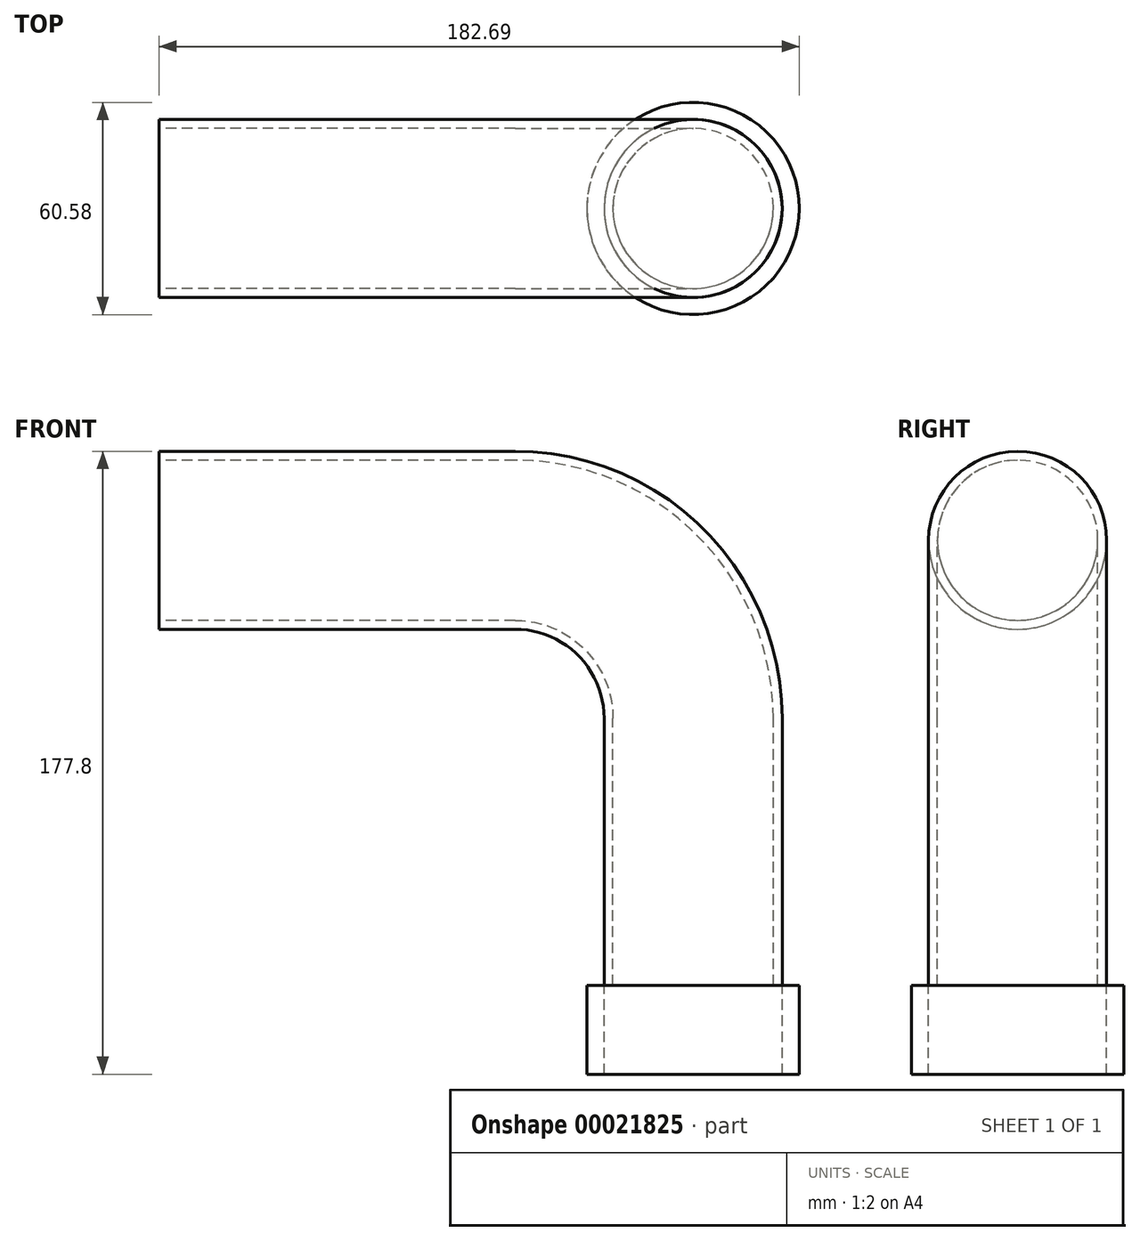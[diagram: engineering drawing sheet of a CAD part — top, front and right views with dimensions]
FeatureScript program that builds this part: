
annotation { "Feature Type Name" : "Feature", "Feature Type Description" : "" }
export const myFeature = defineFeature(function(context is Context, id is Id, definition is map)
    precondition{}
    {
        {
            var Q0;
            Q0=qCreatedBy(makeId("Top.planeOp"),FACE);
            var sketch = newSketch(context, id + "F0", { "sketchPlane" : qUnion([Q0])});
            skCircle(sketch, "E0", {"center": v(0, 0) * mm, "radius": 25.4 * mm});
            skSolve(sketch);
        }
        {
            var Q0;
            Q0=qCreatedBy(makeId("Front.planeOp"),FACE);
            var sketch = newSketch(context, id + "F1", { "sketchPlane" : qUnion([Q0])});
            skLineSegment(sketch, "E1", {"start": v(0, 0) * mm, "end": v(0, 76.2) * mm});
            skLineSegment(sketch, "E2", {"start": v(-50.8, 127) * mm, "end": v(-152.4, 127) * mm});
            skPoint(sketch, "E3.visualSharp", {"position": v(0, 127) * mm});
            skArc(sketch, "E3.filletArc", {"start": v(0, 76.2) * mm, "mid": v(-14.88, 112.12) * mm, "end": v(-50.8, 127) * mm});
            skSolve(sketch);
        }
        {
            var Q0;
            Q0=makeQuery(id+"F0.imprint","IMPRINT",FACE,{"disambiguationData":[TD([[makeQuery(id+"F0.imprint","IMPRINT",EDGE,{"derivedFrom":sQuery(id+"F0.wireOp",EDGE,"E0")}),1.0]])]});
            var Q1;
            Q1=sQuery(id+"F0.wireOp",EDGE,"E0");
            var Q2;
            Q2=sQuery(id+"F1.wireOp",EDGE,"E1");
            var Q3;
            Q3=sQuery(id+"F1.wireOp",EDGE,"E3.filletArc");
            var Q4;
            Q4=sQuery(id+"F1.wireOp",EDGE,"E2");
            sweep(context, id + "F2", {"profiles" : qUnion([Q0]), "surfaceProfiles" : qUnion([Q1]), "path" : qUnion([Q2, Q3, Q4])});
        }
        {
            var Q0;
            Q0=makeQuery(id+"F2.opSweep","CAP_FACE",FACE,{"disambiguationData":[OSD([sQuery(id+"F0.wireOp",EDGE,"E0"),sQuery(id+"F1.wireOp",VERTEX,"E2.end")])],"isStart":false});
            var Q1;
            Q1=makeQuery(id+"F2.opSweep","CAP_FACE",FACE,{"disambiguationData":[OSD([sQuery(id+"F0.wireOp",EDGE,"E0"),sQuery(id+"F1.wireOp",VERTEX,"E1.start")])],"isStart":true});
            shell(context, id + "F3", {"entities" : qUnion([Q0, Q1]), "thickness" : 2.54 * mm});
        }
        {
            var Q0;
            Q0=makeQuery(id+"F2.opSweep","CAP_FACE",FACE,{"disambiguationData":[OSD([sQuery(id+"F0.wireOp",EDGE,"E0"),sQuery(id+"F1.wireOp",VERTEX,"E1.start")])],"isStart":true});
            var sketch = newSketch(context, id + "F4", { "sketchPlane" : qUnion([Q0])});
            skCircle(sketch, "E4.0", {"center": v(0, 0) * mm, "radius": 25.4 * mm});
            skCircle(sketch, "E5", {"center": v(0, 0) * mm, "radius": 30.3 * mm});
            skSolve(sketch);
        }
        {
            var Q0;
            Q0=makeQuery(id+"F4.imprint","IMPRINT",FACE,{"disambiguationData":[TD([[makeQuery(id+"F4.imprint","IMPRINT",EDGE,{"derivedFrom":sQuery(id+"F4.wireOp",EDGE,"E4.0")}),1.0]])]});
            var Q1;
            Q1=sQuery(id+"F4.wireOp",EDGE,"E4.0");
            var Q2;
            Q2=sQuery(id+"F4.wireOp",EDGE,"E5");
            extrude(context, id + "F5", {"entities" : qUnion([Q0]), "surfaceEntities" : qUnion([Q1, Q2]), "depth" : 25.4 * mm});
        }
    });
